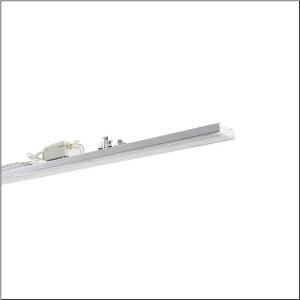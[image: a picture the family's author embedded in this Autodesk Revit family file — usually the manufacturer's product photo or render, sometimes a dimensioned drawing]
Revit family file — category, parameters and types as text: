
# Revit family: licross_r__21_recessed_ho_52tl1edn4dxs_e230
name_source: partatom
category: Lighting Fixtures
units: mm (PartAtom-declared; Revit-internal decimal feet)

## family parameters
Cut with Voids When Loaded = No
Host = Face
Light Source = No
Part Type = Normal
Room Calculation Point = No
Round Connector Dimension = Use Diameter
Shared = No

## types (1)
- --- (1 x LED, 13000 lm, 74.4 W, 4000K)
    Apparent Load = 74 VA
    CIE Flux Codes = 85 95 99 100 100
    Color Rendering = 80
    Color Temperature = 4000K
    Default Elevation = 1800 mm
    Description = Licross® 21 Recessed HO, luminaire insert, of sheet steel, galvanised, coil coated, white, length: 1.500mm, width: 66mm, height: 67mm, LED rated luminous flux: 13.000lm, light colour: 840, control gear: DALI 2, with plug, 5-pole, with phase selection, mains connection: 220..240V, AC, 50/60Hz, rated input power: 74W, halogen-free wiring, primary light control with lens, of plastic, primary optical cover: cover, of PMMA, light emission: direct distribution, primary light characteristic: symmetric, protection rating (complete): IP40, insulation class (complete): insulation class I (protective earthing), certification: CE, ENEC, VDE, UKCA, protection symbol: D if used in an environment without relevant dust loads with corresponding accessories, impact resistance: IK06, permissible ambient temperature for indoor applications: -25..+30°C, corresponds to IFS (International Featured Standards) requirements for safety and quality in the food industry, reducing of maximum allowable ambient temperature of 5°C with ceiling mounting, LABS conformity tested according to VDMA 24364:2018-05, packaging unit: 1 piece
    Height = 58 mm
    Lamp = 1 x LED
    Lamp Light Flux = 13000 lm
    Lamp Power = 74.4 W
    Lamp count = 1
    Length = 1500 mm
    Luminous efficacy = 175 lm/W
    Manufacturer = Siteco
    ModVariant = No
    Model = 52TL1EDN4DXS
    Mounting Place = Ceiling
    Mounting Type = Pendant
    Number of Poles = 1
    OnlyDefault = Yes
    Power Factor = 1
    Product Name = Licross® 21 Recessed HO
    Product group = luminaire insert
    ProductGroupID = 901
    Protection Class = Protection class I
    Protection Degree = IP 40
    RLX_Detail_Level = 1
    RLX_Emergency_Light_Flux = 0 lm
    RLX_Emergency_Type = 0
    RLX_Emergency_Type_DB = No
    RlxData = <blob elided: 24657 chars, md5=4a8cab6c>
    Socket = socket
    Standby Power = 0 W
    System Light Flux = 13000 lm
    System Power = 74 W
    Type Comments = factory setting: luminous flux: 100 % | dim-lin: 254 | 426 mA
    Type Image = l_1296930.jpg
    URL = http://relux.com
    VarID = @adj_056631
    Voltage = 0 V
    Weight = 0.00 kg
    Width = 66 mm

## geometry (parser evidence)
native form markers: Blend x4, Sweep x12
no freeform markers — native parametric forms only
